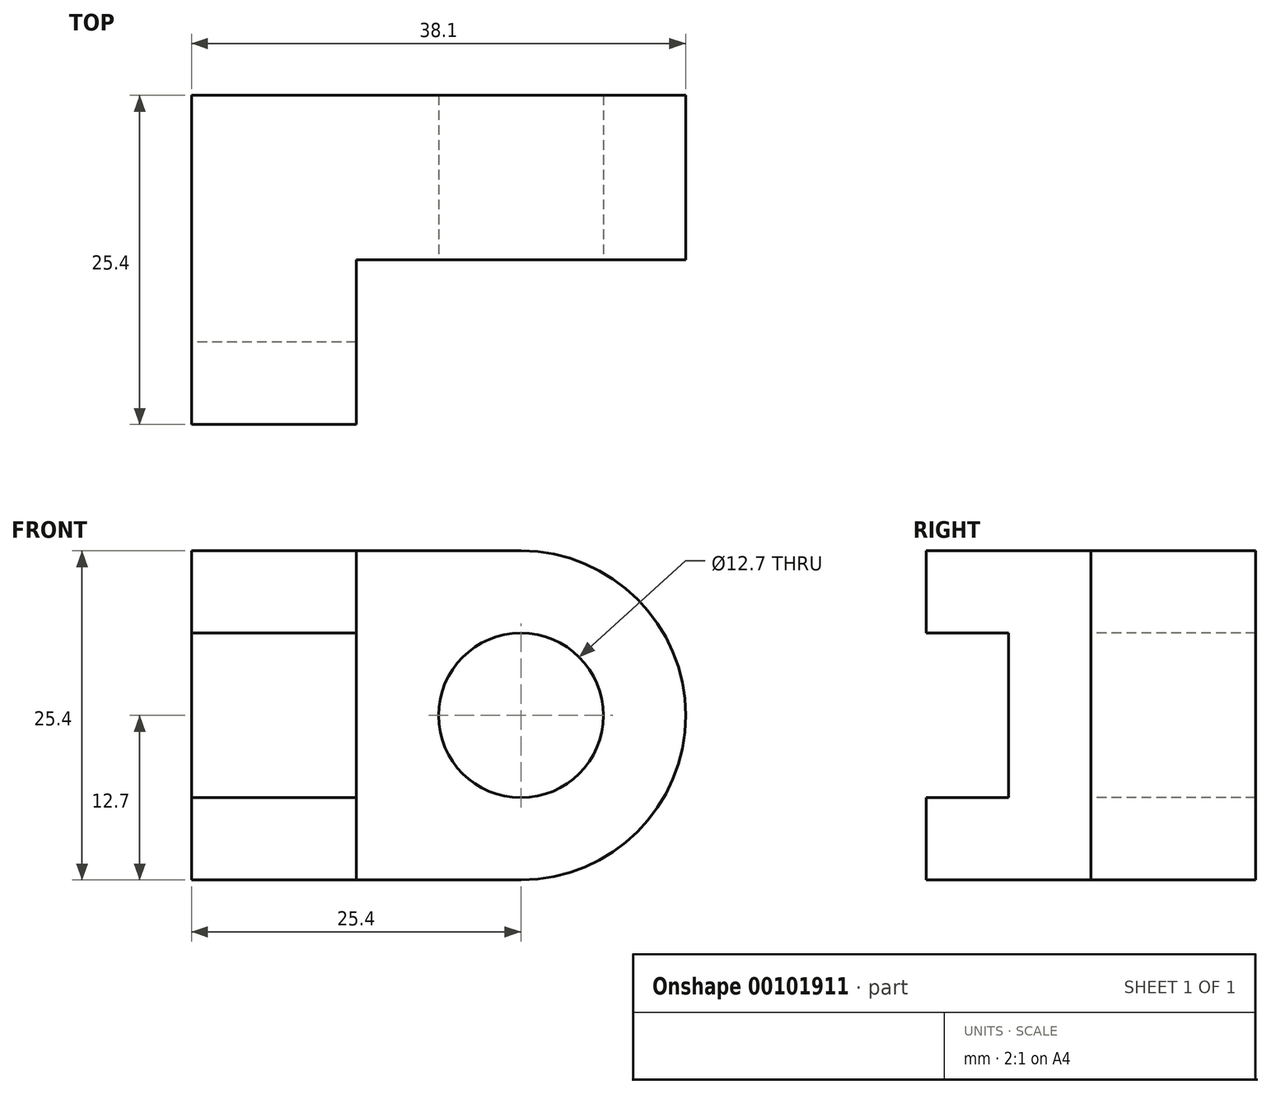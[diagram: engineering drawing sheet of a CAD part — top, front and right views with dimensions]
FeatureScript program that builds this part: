
annotation { "Feature Type Name" : "Feature", "Feature Type Description" : "" }
export const myFeature = defineFeature(function(context is Context, id is Id, definition is map)
    precondition{}
    {
        {
            var Q0;
            Q0=qCreatedBy(makeId("Front.planeOp"),FACE);
            var sketch = newSketch(context, id + "F0", { "sketchPlane" : qUnion([Q0])});
            skLineSegment(sketch, "E0.bottom", {"start": v(0, 0) * mm, "end": v(25.4, 0) * mm});
            skLineSegment(sketch, "E0.top", {"start": v(0, 25.4) * mm, "end": v(25.4, 25.4) * mm});
            skLineSegment(sketch, "E0.left", {"start": v(0, 0) * mm, "end": v(0, 25.4) * mm});
            skArc(sketch, "E1", {"start": v(25.4, 0) * mm, "mid": v(38.1, 12.7) * mm, "end": v(25.4, 25.4) * mm});
            skSolve(sketch);
        }
        {
            var Q0;
            Q0 = qSketchRegion(id + "F0", true);
            extrude(context, id + "F1", {"entities" : qUnion([Q0]), "depth" : 12.7 * mm});
        }
        {
            var Q0;
            Q0=qCreatedBy(makeId("Right.planeOp"),FACE);
            var sketch = newSketch(context, id + "F2", { "sketchPlane" : qUnion([Q0])});
            skLineSegment(sketch, "E2", {"start": v(0, 25.4) * mm, "end": v(-25.4, 25.4) * mm});
            skLineSegment(sketch, "E3", {"start": v(-25.4, 25.4) * mm, "end": v(-25.4, 19.05) * mm});
            skLineSegment(sketch, "E4", {"start": v(-25.4, 19.05) * mm, "end": v(-19.05, 19.05) * mm});
            skLineSegment(sketch, "E5", {"start": v(-19.05, 19.05) * mm, "end": v(-19.05, 6.35) * mm});
            skLineSegment(sketch, "E6", {"start": v(-19.05, 6.35) * mm, "end": v(-25.4, 6.35) * mm});
            skLineSegment(sketch, "E7", {"start": v(-25.4, 6.35) * mm, "end": v(-25.4, 0) * mm});
            skLineSegment(sketch, "E8", {"start": v(-25.4, 0) * mm, "end": v(0, 0) * mm});
            skLineSegment(sketch, "E9", {"start": v(0, 0) * mm, "end": v(0, 25.4) * mm});
            skSolve(sketch);
        }
        {
            var Q0;
            Q0 = qSketchRegion(id + "F2", true);
            extrude(context, id + "F3", {"entities" : qUnion([Q0]), "operationType" : NewBodyOperationType.ADD, "depth" : 12.7 * mm});
        }
        {
            var Q0;
            Q0=makeQuery(id+"F1.opExtrude","CAP_FACE",FACE,{"disambiguationData":[OSD([sQuery(id+"F0.wireOp",EDGE,"E0.bottom"),sQuery(id+"F0.wireOp",EDGE,"E0.top"),sQuery(id+"F0.wireOp",EDGE,"E0.left"),sQuery(id+"F0.wireOp",EDGE,"E1")])],"isStart":false});
            var sketch = newSketch(context, id + "F4", { "sketchPlane" : qUnion([Q0])});
            skCircle(sketch, "E10", {"center": v(25.4, 12.7) * mm, "radius": 6.35 * mm});
            skSolve(sketch);
        }
        {
            var Q0;
            Q0 = qSketchRegion(id + "F4", true);
            extrude(context, id + "F5", {"entities" : qUnion([Q0]), "operationType" : NewBodyOperationType.REMOVE, "endBound" : BoundingType.THROUGH_ALL, "oppositeDirection" : true, "depth" : 25.4 * mm});
        }
    });
